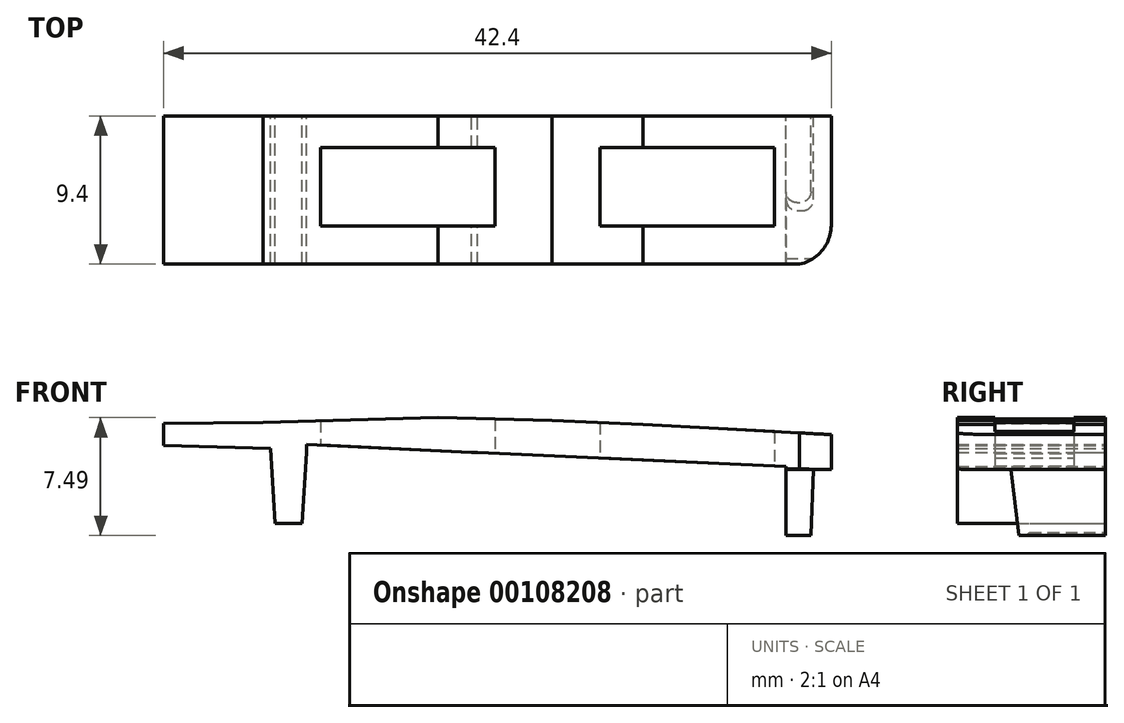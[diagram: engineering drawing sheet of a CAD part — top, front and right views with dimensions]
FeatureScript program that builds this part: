
annotation { "Feature Type Name" : "Feature", "Feature Type Description" : "" }
export const myFeature = defineFeature(function(context is Context, id is Id, definition is map)
    precondition{}
    {
        {
            var Q0;
            Q0=qCreatedBy(makeId("Front.planeOp"),FACE);
            var sketch = newSketch(context, id + "F0", { "sketchPlane" : qUnion([Q0])});
            skLineSegment(sketch, "E0", {"start": v(-49.8, 14.78) * mm, "end": v(-49.8, 13.38) * mm});
            skLineSegment(sketch, "E1", {"start": v(-49.8, 13.38) * mm, "end": v(-43.03, 13.2) * mm});
            skLineSegment(sketch, "E2", {"start": v(-43.03, 13.2) * mm, "end": v(-42.72, 8.42) * mm});
            skLineSegment(sketch, "E3", {"start": v(-41, 8.42) * mm, "end": v(-40.72, 12.95) * mm});
            skLineSegment(sketch, "E4", {"start": v(-40.72, 12.95) * mm, "end": v(-40.72, 13.45) * mm});
            skLineSegment(sketch, "E5", {"start": v(-40.72, 13.45) * mm, "end": v(-30.26, 12.95) * mm});
            skLineSegment(sketch, "E6", {"start": v(-30.26, 12.95) * mm, "end": v(-29.87, 12.93) * mm});
            skLineSegment(sketch, "E7", {"start": v(-29.87, 12.93) * mm, "end": v(-13.84, 12.22) * mm});
            skLineSegment(sketch, "E8", {"start": v(-13.84, 12.22) * mm, "end": v(-10.27, 12.05) * mm});
            skLineSegment(sketch, "E9", {"start": v(-10.27, 12.05) * mm, "end": v(-10.28, 7.85) * mm});
            skLineSegment(sketch, "E10", {"start": v(-8.7, 7.67) * mm, "end": v(-8.52, 11.87) * mm});
            skLineSegment(sketch, "E11", {"start": v(-8.52, 11.87) * mm, "end": v(-7.4, 11.87) * mm});
            skLineSegment(sketch, "E12", {"start": v(-7.4, 11.87) * mm, "end": v(-7.4, 14.07) * mm});
            skLineSegment(sketch, "E13", {"start": v(-7.4, 14.07) * mm, "end": v(-14.56, 14.45) * mm});
            skLineSegment(sketch, "E14", {"start": v(-14.56, 14.45) * mm, "end": v(-19.36, 14.73) * mm});
            skLineSegment(sketch, "E15", {"start": v(-19.36, 14.73) * mm, "end": v(-25.13, 14.97) * mm});
            skLineSegment(sketch, "E16", {"start": v(-25.13, 14.97) * mm, "end": v(-32.37, 15.16) * mm});
            skLineSegment(sketch, "E17", {"start": v(-32.37, 15.16) * mm, "end": v(-43.49, 14.86) * mm});
            skLineSegment(sketch, "E18", {"start": v(-43.49, 14.86) * mm, "end": v(-49.8, 14.78) * mm});
            skLineSegment(sketch, "E19", {"start": v(-25.13, 14.97) * mm, "end": v(-25.13, 12.6) * mm, "construction": true});
            skLineSegment(sketch, "E20", {"start": v(-8.7, 7.67) * mm, "end": v(-10.27, 7.67) * mm});
            skLineSegment(sketch, "E21", {"start": v(-10.27, 7.67) * mm, "end": v(-10.28, 7.85) * mm});
            skLineSegment(sketch, "E22", {"start": v(-41, 8.42) * mm, "end": v(-42.72, 8.42) * mm});
            skSolve(sketch);
        }
        {
            var Q0;
            Q0=makeQuery(id+"F0.imprint","IMPRINT",FACE,{"disambiguationData":[TD([[makeQuery(id+"F0.imprint","IMPRINT",EDGE,{"derivedFrom":sQuery(id+"F0.wireOp",EDGE,"E0")}),1.0]])]});
            extrude(context, id + "F1", {"entities" : qUnion([Q0]), "depth" : 9.4 * mm});
        }
        {
            var Q0;
            Q0=qCreatedBy(makeId("Top.planeOp"),FACE);
            var sketch = newSketch(context, id + "F2", { "sketchPlane" : qUnion([Q0])});
            skLineSegment(sketch, "E23", {"start": v(-7.4, -4.7) * mm, "end": v(-11, -4.7) * mm, "construction": true});
            skLineSegment(sketch, "E24", {"start": v(-12.29, 0) * mm, "end": v(-12.29, -2) * mm, "construction": true});
            skLineSegment(sketch, "E25.bottom", {"start": v(-11, -2) * mm, "end": v(-22.1, -2) * mm});
            skLineSegment(sketch, "E25.top", {"start": v(-11, -7) * mm, "end": v(-22.1, -7) * mm});
            skLineSegment(sketch, "E25.left", {"start": v(-11, -2) * mm, "end": v(-11, -7) * mm});
            skLineSegment(sketch, "E25.right", {"start": v(-22.1, -2) * mm, "end": v(-22.1, -7) * mm});
            skLineSegment(sketch, "E26", {"start": v(-22.1, -4.5) * mm, "end": v(-28.75, -4.5) * mm, "construction": true});
            skLineSegment(sketch, "E27", {"start": v(-31.12, 0) * mm, "end": v(-31.12, -2) * mm, "construction": true});
            skLineSegment(sketch, "E28.bottom", {"start": v(-28.75, -2) * mm, "end": v(-39.85, -2) * mm});
            skLineSegment(sketch, "E28.top", {"start": v(-28.75, -7) * mm, "end": v(-39.85, -7) * mm});
            skLineSegment(sketch, "E28.left", {"start": v(-28.75, -2) * mm, "end": v(-28.75, -7) * mm});
            skLineSegment(sketch, "E28.right", {"start": v(-39.85, -2) * mm, "end": v(-39.85, -7) * mm});
            skSolve(sketch);
        }
        {
            var Q0;
            Q0=makeQuery(id+"F2.imprint","IMPRINT",FACE,{"disambiguationData":[TD([[makeQuery(id+"F2.imprint","IMPRINT",EDGE,{"derivedFrom":sQuery(id+"F2.wireOp",EDGE,"E25.bottom")}),1.0]])]});
            var Q1;
            Q1=makeQuery(id+"F2.imprint","IMPRINT",FACE,{"disambiguationData":[TD([[makeQuery(id+"F2.imprint","IMPRINT",EDGE,{"derivedFrom":sQuery(id+"F2.wireOp",EDGE,"E28.bottom")}),1.0]])]});
            extrude(context, id + "F3", {"entities" : qUnion([Q0, Q1]), "operationType" : NewBodyOperationType.REMOVE, "depth" : 21.03 * mm});
        }
        {
            var Q0;
            Q0=qCreatedBy(makeId("Top.planeOp"),FACE);
            var sketch = newSketch(context, id + "F4", { "sketchPlane" : qUnion([Q0])});
            skLineSegment(sketch, "E29", {"start": v(-7.4, -5.97) * mm, "end": v(-7.4, -6.95) * mm});
            skLineSegment(sketch, "E30", {"start": v(-9.9, -9.45) * mm, "end": v(-10.23, -9.45) * mm});
            skLineSegment(sketch, "E31", {"start": v(-10.23, -9.45) * mm, "end": v(-10.23, -13.29) * mm});
            skLineSegment(sketch, "E32", {"start": v(-10.23, -13.29) * mm, "end": v(-4.17, -13.29) * mm});
            skLineSegment(sketch, "E33", {"start": v(-4.17, -13.29) * mm, "end": v(-4.17, -5.88) * mm});
            skLineSegment(sketch, "E34", {"start": v(-4.17, -5.88) * mm, "end": v(-7.4, -5.97) * mm});
            skPoint(sketch, "E35.visualSharp", {"position": v(-7.4, -9.45) * mm});
            skArc(sketch, "E35.filletArc", {"start": v(-9.9, -9.45) * mm, "mid": v(-8.14, -8.72) * mm, "end": v(-7.4, -6.95) * mm});
            skPoint(sketch, "E36.orphan", {"position": v(-7.4, -9.4) * mm});
            skSolve(sketch);
        }
        {
            var Q0;
            Q0=makeQuery(id+"F4.imprint","IMPRINT",FACE,{"disambiguationData":[TD([[makeQuery(id+"F4.imprint","IMPRINT",EDGE,{"derivedFrom":sQuery(id+"F4.wireOp",EDGE,"E29")}),1.0]])]});
            extrude(context, id + "F5", {"entities" : qUnion([Q0]), "operationType" : NewBodyOperationType.REMOVE, "depth" : 33.13 * mm});
        }
        {
            var Q0;
            Q0=qCreatedBy(makeId("Right.planeOp"),FACE);
            var sketch = newSketch(context, id + "F6", { "sketchPlane" : qUnion([Q0])});
            skLineSegment(sketch, "E37", {"start": v(-6, 11.87) * mm, "end": v(-5.5, 7.67) * mm});
            skLineSegment(sketch, "E38", {"start": v(-5.5, 7.67) * mm, "end": v(-9.14, 7.67) * mm});
            skLineSegment(sketch, "E39", {"start": v(-6, 11.87) * mm, "end": v(-9.03, 11.87) * mm});
            skLineSegment(sketch, "E40.0", {"start": v(-9.4, 14.18) * mm, "end": v(-9.4, 11.88) * mm});
            skLineSegment(sketch, "E41", {"start": v(-9.03, 11.87) * mm, "end": v(-9.4, 11.88) * mm});
            skPoint(sketch, "E42.orphan", {"position": v(-9.4, 7.67) * mm});
            skLineSegment(sketch, "E43", {"start": v(-9.4, 11.88) * mm, "end": v(-9.4, 7.67) * mm});
            skLineSegment(sketch, "E44", {"start": v(-9.4, 7.67) * mm, "end": v(-9.14, 7.67) * mm});
            skSolve(sketch);
        }
        {
            var Q0;
            Q0=makeQuery(id+"F6.imprint","IMPRINT",FACE,{"disambiguationData":[TD([[makeQuery(id+"F6.imprint","IMPRINT",EDGE,{"derivedFrom":sQuery(id+"F6.wireOp",EDGE,"E37")}),-1.0]])]});
            extrude(context, id + "F7", {"entities" : qUnion([Q0]), "operationType" : NewBodyOperationType.REMOVE, "oppositeDirection" : true, "depth" : 16.64 * mm});
        }
        {
            var Q0;
            Q0=makeQuery(id+"F7.boolean.opBoolean","INTERSECT",EDGE,{"derivedFrom":[makeQuery(id+"F1.opExtrude","SWEPT_FACE",FACE,{"disambiguationData":[OSD([sQuery(id+"F0.wireOp",EDGE,"E10")])]}),makeQuery(id+"F7.opExtrude","SWEPT_FACE",FACE,{"disambiguationData":[OSD([sQuery(id+"F6.wireOp",EDGE,"E37")])]})]});
            var Q1;
            Q1=makeQuery(id+"F7.boolean.opBoolean","INTERSECT",EDGE,{"derivedFrom":[makeQuery(id+"F1.opExtrude","SWEPT_FACE",FACE,{"disambiguationData":[OSD([sQuery(id+"F0.wireOp",EDGE,"E9")])]}),makeQuery(id+"F7.opExtrude","SWEPT_FACE",FACE,{"disambiguationData":[OSD([sQuery(id+"F6.wireOp",EDGE,"E37")])]})]});
            fillet(context, id + "F8", {"entities" : qUnion([Q0, Q1]), "radius" : .7 * mm, "tangentPropagation" : true, "allowEdgeOverflow" : false});
        }
    });
